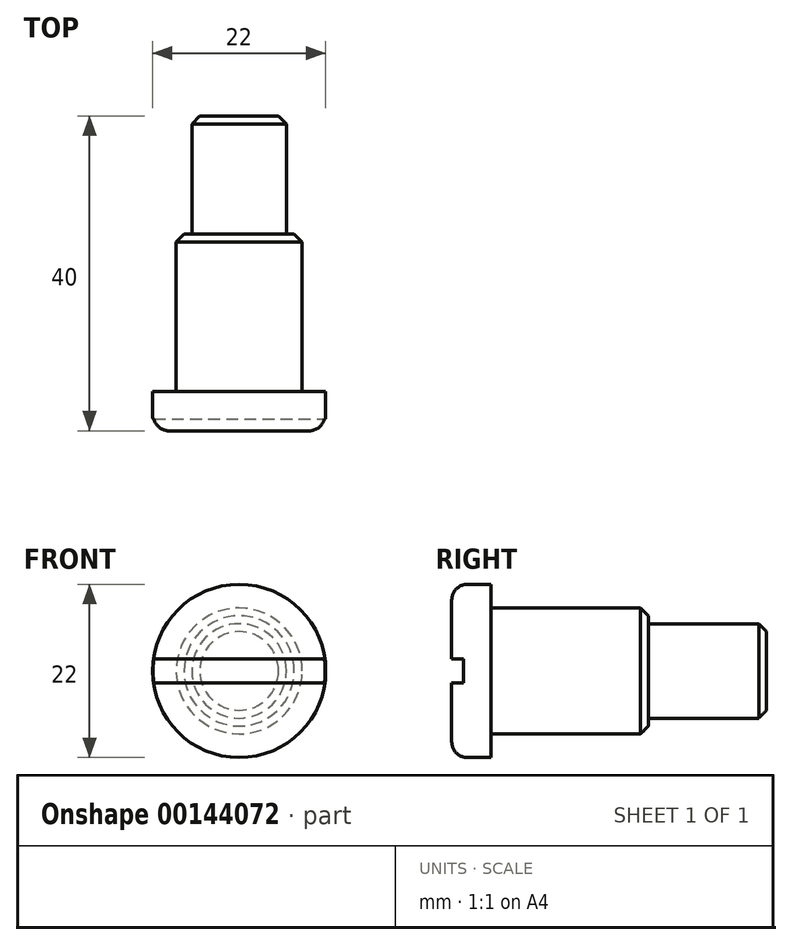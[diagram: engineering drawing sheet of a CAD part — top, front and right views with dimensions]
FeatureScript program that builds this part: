
annotation { "Feature Type Name" : "Feature", "Feature Type Description" : "" }
export const myFeature = defineFeature(function(context is Context, id is Id, definition is map)
    precondition{}
    {
        {
            var Q0;
            Q0=qCreatedBy(makeId("Front.planeOp"),FACE);
            var sketch = newSketch(context, id + "F0", { "sketchPlane" : qUnion([Q0])});
            skCircle(sketch, "E0", {"center": v(0, 0) * mm, "radius": 11 * mm});
            skSolve(sketch);
        }
        {
            var Q0;
            Q0 = qSketchRegion(id + "F0", true);
            extrude(context, id + "F1", {"entities" : qUnion([Q0]), "depth" : 5 * mm});
        }
        {
            var Q0;
            Q0=makeQuery(id+"F1.opExtrude","CAP_EDGE",EDGE,{"disambiguationData":[OSD([sQuery(id+"F0.wireOp",EDGE,"E0")])],"isStart":false});
            fillet(context, id + "F2", {"entities" : qUnion([Q0]), "radius" : 2 * mm, "tangentPropagation" : true, "allowEdgeOverflow" : false});
        }
        {
            var Q0;
            Q0=qCreatedBy(makeId("Front.planeOp"),FACE);
            var sketch = newSketch(context, id + "F3", { "sketchPlane" : qUnion([Q0])});
            skCircle(sketch, "E1", {"center": v(0, 0) * mm, "radius": 8 * mm});
            skCircle(sketch, "E2", {"center": v(0, 0) * mm, "radius": 6 * mm});
            skSolve(sketch);
        }
        {
            var Q0;
            Q0 = qSketchRegion(id + "F3", true);
            extrude(context, id + "F4", {"entities" : qUnion([Q0]), "operationType" : NewBodyOperationType.ADD, "oppositeDirection" : true, "depth" : 20 * mm});
        }
        {
            var Q0;
            Q0=makeQuery(id+"F4.boolean.opBoolean","SPLIT",FACE,{"disambiguationData":[TD([makeQuery(id+"F4.opExtrude","SWEPT_FACE",FACE,{"disambiguationData":[OSD([sQuery(id+"F3.wireOp",EDGE,"E2")])]})])],"derivedFrom":makeQuery(id+"F1.opExtrude","CAP_FACE",FACE,{"disambiguationData":[OSD([sQuery(id+"F0.wireOp",EDGE,"E0")])],"isStart":true})});
            extrude(context, id + "F5", {"entities" : qUnion([Q0]), "operationType" : NewBodyOperationType.ADD, "depth" : 35 * mm});
        }
        {
            var Q0;
            Q0=makeQuery(id+"F5.opExtrude","CAP_EDGE",EDGE,{"disambiguationData":[OSD([sQuery(id+"F3.wireOp",EDGE,"E2")])],"isStart":false});
            var Q1;
            Q1=makeQuery(id+"F4.opExtrude","CAP_EDGE",EDGE,{"disambiguationData":[OSD([sQuery(id+"F3.wireOp",EDGE,"E1")])],"isStart":false});
            chamfer(context, id + "F6", {"entities" : qUnion([Q0, Q1]), "chamferType" : ChamferType.OFFSET_ANGLE, "width" : 1 * mm, "oppositeDirection" : false, "angle" : 45 * degree, "tangentPropagation" : true});
        }
        {
            var Q0;
            Q0=qCreatedBy(makeId("Right.planeOp"),FACE);
            var sketch = newSketch(context, id + "F7", { "sketchPlane" : qUnion([Q0])});
            skLineSegment(sketch, "E3.0", {"start": v(-5, -9) * mm, "end": v(-5, -1.5) * mm, "construction": true});
            skLineSegment(sketch, "E4.0", {"start": v(-3, 11) * mm, "end": v(-3, -11) * mm, "construction": true});
            skArc(sketch, "E5", {"start": v(-5, -9) * mm, "mid": v(-4.41, -10.41) * mm, "end": v(-3, -11) * mm, "construction": true});
            skArc(sketch, "E6", {"start": v(-3, 11) * mm, "mid": v(-4.41, 10.41) * mm, "end": v(-5, 9) * mm, "construction": true});
            skLineSegment(sketch, "E7", {"start": v(-3, 11) * mm, "end": v(0, 11) * mm, "construction": true});
            skLineSegment(sketch, "E8", {"start": v(0, -11) * mm, "end": v(-3, -11) * mm, "construction": true});
            skLineSegment(sketch, "E9", {"start": v(-5, 1.5) * mm, "end": v(-3.5, 1.5) * mm});
            skLineSegment(sketch, "E10", {"start": v(-3.5, 1.5) * mm, "end": v(-3.5, -1.5) * mm});
            skLineSegment(sketch, "E11", {"start": v(-3.5, -1.5) * mm, "end": v(-5, -1.5) * mm});
            skLineSegment(sketch, "E12.trimOffspring", {"start": v(-5, 1.5) * mm, "end": v(-5, 9) * mm, "construction": true});
            skLineSegment(sketch, "E13", {"start": v(-5, 1.5) * mm, "end": v(-5, -1.5) * mm});
            skSolve(sketch);
        }
        {
            var Q0;
            Q0=makeQuery(id+"F7.imprint","IMPRINT",FACE,{"disambiguationData":[TD([[makeQuery(id+"F7.imprint","IMPRINT",EDGE,{"derivedFrom":sQuery(id+"F7.wireOp",EDGE,"E9")}),-1.0]])]});
            extrude(context, id + "F8", {"entities" : qUnion([Q0]), "operationType" : NewBodyOperationType.REMOVE, "endBound" : BoundingType.SYMMETRIC, "oppositeDirection" : true, "depth" : 25 * mm});
        }
    });
